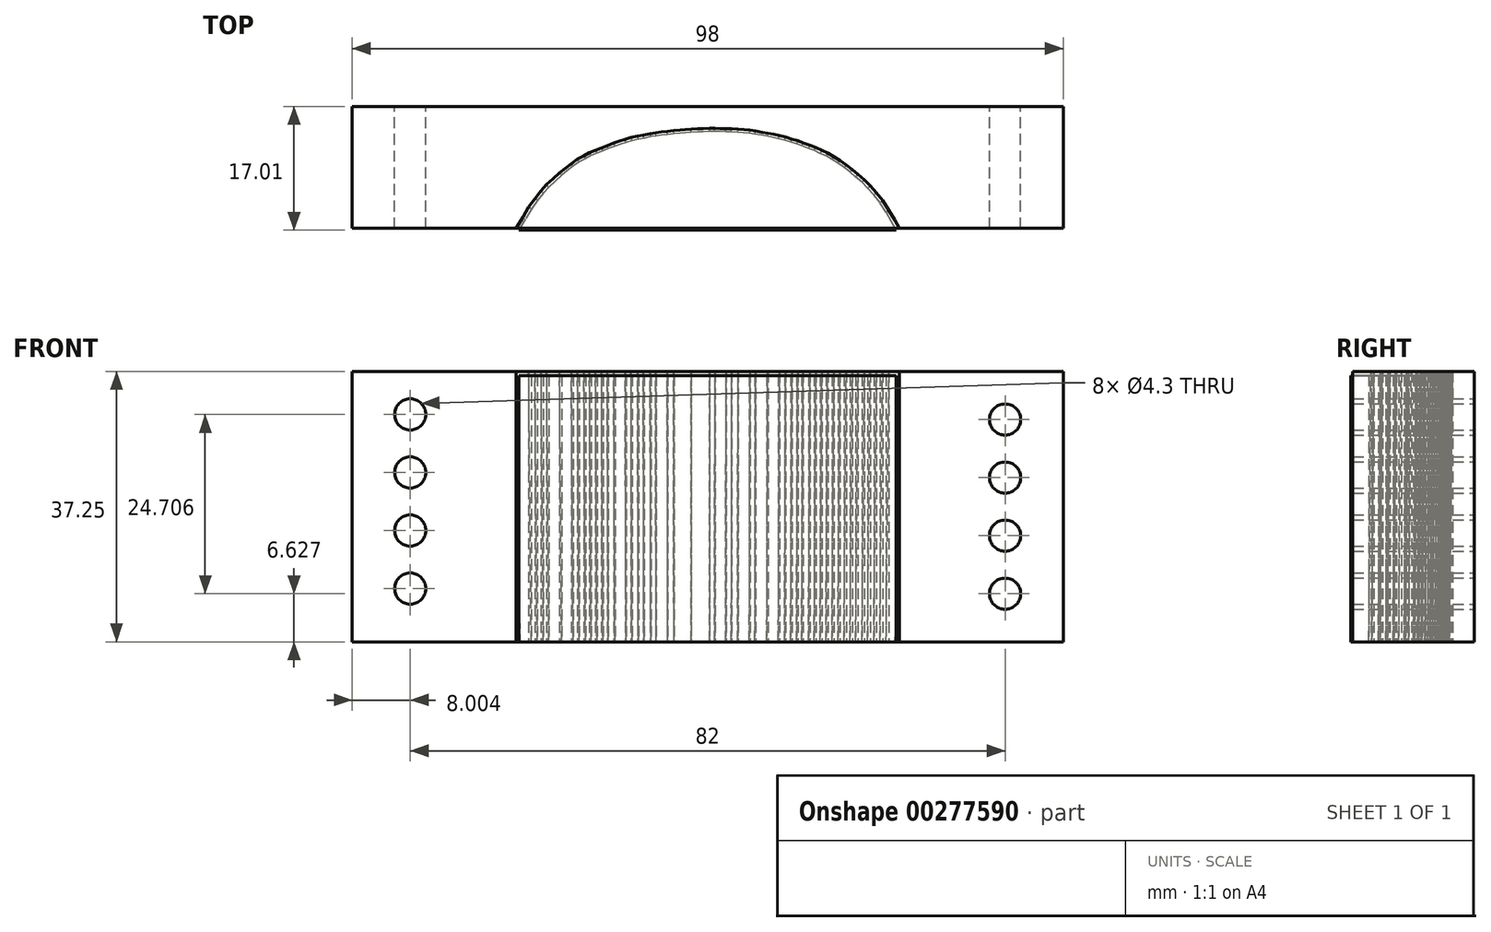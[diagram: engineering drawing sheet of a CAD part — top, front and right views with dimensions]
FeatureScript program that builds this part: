
annotation { "Feature Type Name" : "Feature", "Feature Type Description" : "" }
export const myFeature = defineFeature(function(context is Context, id is Id, definition is map)
    precondition{}
    {
        {
            var Q0;
            Q0=qCreatedBy(makeId("Top.planeOp"),FACE);
            var sketch = newSketch(context, id + "F0", { "sketchPlane" : qUnion([Q0])});
            skLineSegment(sketch, "E0", {"start": v(-9.94, -1.75) * mm, "end": v(-10.2, -1.18) * mm});
            skLineSegment(sketch, "E1", {"start": v(-10.2, -1.18) * mm, "end": v(-10.52, -0.6) * mm});
            skLineSegment(sketch, "E2", {"start": v(-10.52, -0.6) * mm, "end": v(-10.8, -0.09) * mm});
            skLineSegment(sketch, "E3", {"start": v(-10.8, -0.09) * mm, "end": v(-11.13, 0.42) * mm});
            skLineSegment(sketch, "E4", {"start": v(-11.13, 0.42) * mm, "end": v(-11.45, 0.82) * mm});
            skLineSegment(sketch, "E5", {"start": v(-11.45, 0.82) * mm, "end": v(-11.77, 1.2) * mm});
            skLineSegment(sketch, "E6", {"start": v(-11.77, 1.2) * mm, "end": v(-12.06, 1.5) * mm});
            skLineSegment(sketch, "E7", {"start": v(-12.06, 1.5) * mm, "end": v(-12.4, 1.78) * mm});
            skLineSegment(sketch, "E8", {"start": v(-12.4, 1.78) * mm, "end": v(-12.7, 2.03) * mm});
            skLineSegment(sketch, "E9", {"start": v(-12.7, 2.03) * mm, "end": v(-13.01, 2.28) * mm});
            skLineSegment(sketch, "E10", {"start": v(-13.01, 2.28) * mm, "end": v(-13.33, 2.5) * mm});
            skLineSegment(sketch, "E11", {"start": v(-13.33, 2.5) * mm, "end": v(-13.64, 2.7) * mm});
            skLineSegment(sketch, "E12", {"start": v(-13.64, 2.7) * mm, "end": v(-13.96, 2.9) * mm});
            skLineSegment(sketch, "E13", {"start": v(-13.96, 2.9) * mm, "end": v(-14.27, 3.04) * mm});
            skLineSegment(sketch, "E14", {"start": v(-14.27, 3.04) * mm, "end": v(-14.58, 3.2) * mm});
            skLineSegment(sketch, "E15", {"start": v(-14.58, 3.2) * mm, "end": v(-14.88, 3.3) * mm});
            skLineSegment(sketch, "E16", {"start": v(-14.88, 3.3) * mm, "end": v(-15.24, 3.44) * mm});
            skLineSegment(sketch, "E17", {"start": v(-15.24, 3.44) * mm, "end": v(-15.51, 3.55) * mm});
            skLineSegment(sketch, "E18", {"start": v(-15.51, 3.55) * mm, "end": v(-15.82, 3.64) * mm});
            skLineSegment(sketch, "E19", {"start": v(-15.82, 3.64) * mm, "end": v(-16.14, 3.75) * mm});
            skLineSegment(sketch, "E20", {"start": v(-16.14, 3.75) * mm, "end": v(-16.47, 3.83) * mm});
            skLineSegment(sketch, "E21", {"start": v(-16.47, 3.83) * mm, "end": v(-16.76, 3.9) * mm});
            skLineSegment(sketch, "E22", {"start": v(-16.76, 3.9) * mm, "end": v(-17.07, 3.96) * mm});
            skLineSegment(sketch, "E23", {"start": v(-17.07, 3.96) * mm, "end": v(-17.36, 4.01) * mm});
            skLineSegment(sketch, "E24", {"start": v(-17.36, 4.01) * mm, "end": v(-17.7, 4.07) * mm});
            skLineSegment(sketch, "E25", {"start": v(-17.7, 4.07) * mm, "end": v(-18, 4.12) * mm});
            skLineSegment(sketch, "E26", {"start": v(-18, 4.12) * mm, "end": v(-18.32, 4.15) * mm});
            skLineSegment(sketch, "E27", {"start": v(-18.32, 4.15) * mm, "end": v(-18.62, 4.18) * mm});
            skLineSegment(sketch, "E28", {"start": v(-18.62, 4.18) * mm, "end": v(-18.94, 4.2) * mm});
            skLineSegment(sketch, "E29", {"start": v(-18.94, 4.2) * mm, "end": v(-19.25, 4.2) * mm});
            skLineSegment(sketch, "E30", {"start": v(-19.25, 4.2) * mm, "end": v(-19.55, 4.22) * mm});
            skLineSegment(sketch, "E31", {"start": v(-19.55, 4.22) * mm, "end": v(-19.82, 4.23) * mm});
            skLineSegment(sketch, "E32", {"start": v(-19.82, 4.23) * mm, "end": v(-20.1, 4.24) * mm});
            skLineSegment(sketch, "E33", {"start": v(-20.1, 4.24) * mm, "end": v(-20.44, 4.23) * mm});
            skLineSegment(sketch, "E34", {"start": v(-20.44, 4.23) * mm, "end": v(-20.73, 4.21) * mm});
            skLineSegment(sketch, "E35", {"start": v(-20.73, 4.21) * mm, "end": v(-21.06, 4.2) * mm});
            skLineSegment(sketch, "E36", {"start": v(-21.06, 4.2) * mm, "end": v(-21.37, 4.18) * mm});
            skLineSegment(sketch, "E37", {"start": v(-21.37, 4.18) * mm, "end": v(-21.64, 4.16) * mm});
            skLineSegment(sketch, "E38", {"start": v(-21.64, 4.16) * mm, "end": v(-21.98, 4.13) * mm});
            skLineSegment(sketch, "E39", {"start": v(-21.98, 4.13) * mm, "end": v(-22.3, 4.1) * mm});
            skLineSegment(sketch, "E40", {"start": v(-22.3, 4.1) * mm, "end": v(-22.62, 4.06) * mm});
            skLineSegment(sketch, "E41", {"start": v(-22.62, 4.06) * mm, "end": v(-22.92, 4.02) * mm});
            skLineSegment(sketch, "E42", {"start": v(-22.92, 4.02) * mm, "end": v(-23.2, 3.98) * mm});
            skLineSegment(sketch, "E43", {"start": v(-23.2, 3.98) * mm, "end": v(-23.56, 3.9) * mm});
            skLineSegment(sketch, "E44", {"start": v(-23.56, 3.9) * mm, "end": v(-23.86, 3.86) * mm});
            skLineSegment(sketch, "E45", {"start": v(-23.86, 3.86) * mm, "end": v(-24.2, 3.79) * mm});
            skLineSegment(sketch, "E46", {"start": v(-24.2, 3.79) * mm, "end": v(-24.5, 3.69) * mm});
            skLineSegment(sketch, "E47", {"start": v(-24.5, 3.69) * mm, "end": v(-24.8, 3.6) * mm});
            skLineSegment(sketch, "E48", {"start": v(-24.8, 3.6) * mm, "end": v(-25.1, 3.5) * mm});
            skLineSegment(sketch, "E49", {"start": v(-25.1, 3.5) * mm, "end": v(-25.44, 3.38) * mm});
            skLineSegment(sketch, "E50", {"start": v(-25.44, 3.38) * mm, "end": v(-25.73, 3.25) * mm});
            skLineSegment(sketch, "E51", {"start": v(-25.73, 3.25) * mm, "end": v(-26.05, 3.13) * mm});
            skLineSegment(sketch, "E52", {"start": v(-26.05, 3.13) * mm, "end": v(-26.36, 3.01) * mm});
            skLineSegment(sketch, "E53", {"start": v(-26.36, 3.01) * mm, "end": v(-26.66, 2.86) * mm});
            skLineSegment(sketch, "E54", {"start": v(-26.66, 2.86) * mm, "end": v(-26.99, 2.67) * mm});
            skLineSegment(sketch, "E55", {"start": v(-26.99, 2.67) * mm, "end": v(-27.31, 2.46) * mm});
            skLineSegment(sketch, "E56", {"start": v(-27.31, 2.46) * mm, "end": v(-27.61, 2.22) * mm});
            skLineSegment(sketch, "E57", {"start": v(-27.61, 2.22) * mm, "end": v(-27.92, 1.98) * mm});
            skLineSegment(sketch, "E58", {"start": v(-27.92, 1.98) * mm, "end": v(-28.27, 1.67) * mm});
            skLineSegment(sketch, "E59", {"start": v(-28.27, 1.67) * mm, "end": v(-28.6, 1.37) * mm});
            skLineSegment(sketch, "E60", {"start": v(-28.6, 1.37) * mm, "end": v(-28.89, 1.04) * mm});
            skLineSegment(sketch, "E61", {"start": v(-28.89, 1.04) * mm, "end": v(-29.22, 0.65) * mm});
            skLineSegment(sketch, "E62", {"start": v(-29.22, 0.65) * mm, "end": v(-29.54, 0.2) * mm});
            skLineSegment(sketch, "E63", {"start": v(-29.54, 0.2) * mm, "end": v(-29.85, -0.3) * mm});
            skLineSegment(sketch, "E64", {"start": v(-29.85, -0.3) * mm, "end": v(-30.2, -0.9) * mm});
            skLineSegment(sketch, "E65", {"start": v(-30.2, -0.9) * mm, "end": v(-30.45, -1.56) * mm});
            skLineSegment(sketch, "E66", {"start": v(-30.45, -1.56) * mm, "end": v(-9.94, -1.75) * mm, "construction": true});
            skLineSegment(sketch, "E67", {"start": v(-32.25, 10.07) * mm, "end": v(-9.38, 9.9) * mm, "construction": true});
            skLineSegment(sketch, "E68", {"start": v(-32.25, 10.07) * mm, "end": v(-30.45, -1.56) * mm, "construction": true});
            skLineSegment(sketch, "E69", {"start": v(-30.45, -1.56) * mm, "end": v(-9.38, 9.9) * mm, "construction": true});
            skLineSegment(sketch, "E70", {"start": v(-9.38, 9.9) * mm, "end": v(-9.94, -1.75) * mm, "construction": true});
            skLineSegment(sketch, "E71", {"start": v(-33.87, 11.08) * mm, "end": v(-32.25, 10.07) * mm, "construction": true});
            skLineSegment(sketch, "E72", {"start": v(-32.25, 10.07) * mm, "end": v(-7.89, 11.08) * mm, "construction": true});
            skLineSegment(sketch, "E73", {"start": v(-30.2, -0.9) * mm, "end": v(-10.28, -1.04) * mm});
            skLineSegment(sketch, "E74", {"start": v(-32.25, 10.07) * mm, "end": v(-22.42, 10.07) * mm, "construction": true});
            skPoint(sketch, "E75", {"position": v(-20.66, -0.96) * mm});
            skLineSegment(sketch, "E76", {"start": v(-20.62, 4.22) * mm, "end": v(-20.7, -7) * mm, "construction": true});
            skPoint(sketch, "E77", {"position": v(-20.7, -7) * mm});
            skSolve(sketch);
        }
        {
            var Q0;
            {var subQ0=sQuery(id+"F0.wireOp",EDGE,"E2");Q0=makeQuery(id+"F0.imprint","IMPRINT",FACE,{"disambiguationData":[TD([[makeQuery(id+"F0.imprint","IMPRINT",EDGE,{"derivedFrom":subQ0}),1.0]])]});}
            extrude(context, id + "F1", {"entities" : qUnion([Q0]), "depth" : 38.1 * mm * .369});
        }
        {
            var Q0;
            Q0=makeQuery(id+"F1.opExtrude","SWEPT_BODY",BODY,{"disambiguationData":[OSD([sQuery(id+"F0.wireOp",EDGE,"E1"),sQuery(id+"F0.wireOp",EDGE,"E2"),sQuery(id+"F0.wireOp",EDGE,"E3"),sQuery(id+"F0.wireOp",EDGE,"E4"),sQuery(id+"F0.wireOp",EDGE,"E5"),sQuery(id+"F0.wireOp",EDGE,"E6"),sQuery(id+"F0.wireOp",EDGE,"E7"),sQuery(id+"F0.wireOp",EDGE,"E8"),sQuery(id+"F0.wireOp",EDGE,"E9"),sQuery(id+"F0.wireOp",EDGE,"E10"),sQuery(id+"F0.wireOp",EDGE,"E11"),sQuery(id+"F0.wireOp",EDGE,"E12"),sQuery(id+"F0.wireOp",EDGE,"E13"),sQuery(id+"F0.wireOp",EDGE,"E14"),sQuery(id+"F0.wireOp",EDGE,"E15"),sQuery(id+"F0.wireOp",EDGE,"E16"),sQuery(id+"F0.wireOp",EDGE,"E17"),sQuery(id+"F0.wireOp",EDGE,"E18"),sQuery(id+"F0.wireOp",EDGE,"E19"),sQuery(id+"F0.wireOp",EDGE,"E20"),sQuery(id+"F0.wireOp",EDGE,"E21"),sQuery(id+"F0.wireOp",EDGE,"E22"),sQuery(id+"F0.wireOp",EDGE,"E23"),sQuery(id+"F0.wireOp",EDGE,"E24"),sQuery(id+"F0.wireOp",EDGE,"E25"),sQuery(id+"F0.wireOp",EDGE,"E26"),sQuery(id+"F0.wireOp",EDGE,"E27"),sQuery(id+"F0.wireOp",EDGE,"E28"),sQuery(id+"F0.wireOp",EDGE,"E29"),sQuery(id+"F0.wireOp",EDGE,"E30"),sQuery(id+"F0.wireOp",EDGE,"E31"),sQuery(id+"F0.wireOp",EDGE,"E32"),sQuery(id+"F0.wireOp",EDGE,"E33"),sQuery(id+"F0.wireOp",EDGE,"E34"),sQuery(id+"F0.wireOp",EDGE,"E35"),sQuery(id+"F0.wireOp",EDGE,"E36"),sQuery(id+"F0.wireOp",EDGE,"E37"),sQuery(id+"F0.wireOp",EDGE,"E38"),sQuery(id+"F0.wireOp",EDGE,"E39"),sQuery(id+"F0.wireOp",EDGE,"E40"),sQuery(id+"F0.wireOp",EDGE,"E41"),sQuery(id+"F0.wireOp",EDGE,"E42"),sQuery(id+"F0.wireOp",EDGE,"E43"),sQuery(id+"F0.wireOp",EDGE,"E44"),sQuery(id+"F0.wireOp",EDGE,"E45"),sQuery(id+"F0.wireOp",EDGE,"E46"),sQuery(id+"F0.wireOp",EDGE,"E47"),sQuery(id+"F0.wireOp",EDGE,"E48"),sQuery(id+"F0.wireOp",EDGE,"E49"),sQuery(id+"F0.wireOp",EDGE,"E50"),sQuery(id+"F0.wireOp",EDGE,"E51"),sQuery(id+"F0.wireOp",EDGE,"E52"),sQuery(id+"F0.wireOp",EDGE,"E53"),sQuery(id+"F0.wireOp",EDGE,"E54"),sQuery(id+"F0.wireOp",EDGE,"E55"),sQuery(id+"F0.wireOp",EDGE,"E56"),sQuery(id+"F0.wireOp",EDGE,"E57"),sQuery(id+"F0.wireOp",EDGE,"E58"),sQuery(id+"F0.wireOp",EDGE,"E59"),sQuery(id+"F0.wireOp",EDGE,"E60"),sQuery(id+"F0.wireOp",EDGE,"E61"),sQuery(id+"F0.wireOp",EDGE,"E62"),sQuery(id+"F0.wireOp",EDGE,"E63"),sQuery(id+"F0.wireOp",EDGE,"E64"),sQuery(id+"F0.wireOp",EDGE,"E73")])]});
            var Q1;
            Q1=makeQuery(id+"F1.opExtrude","SWEPT_EDGE",EDGE,{"disambiguationData":[OSD([sQuery(id+"F0.wireOp",EDGE,"E64"),sQuery(id+"F0.wireOp",EDGE,"E73")])]});
            transform(context, id + "F2", {"entities" : qUnion([Q0]), "transformType" : TransformType.ROTATION, "transformAxis" : qUnion([Q1]), "angle" : .43 * degree, "oppositeDirection" : true, "makeCopy" : false});
        }
        {
            var Q0;
            Q0=makeQuery(id+"F1.opExtrude","SWEPT_BODY",BODY,{"disambiguationData":[OSD([sQuery(id+"F0.wireOp",EDGE,"E1"),sQuery(id+"F0.wireOp",EDGE,"E2"),sQuery(id+"F0.wireOp",EDGE,"E3"),sQuery(id+"F0.wireOp",EDGE,"E4"),sQuery(id+"F0.wireOp",EDGE,"E5"),sQuery(id+"F0.wireOp",EDGE,"E6"),sQuery(id+"F0.wireOp",EDGE,"E7"),sQuery(id+"F0.wireOp",EDGE,"E8"),sQuery(id+"F0.wireOp",EDGE,"E9"),sQuery(id+"F0.wireOp",EDGE,"E10"),sQuery(id+"F0.wireOp",EDGE,"E11"),sQuery(id+"F0.wireOp",EDGE,"E12"),sQuery(id+"F0.wireOp",EDGE,"E13"),sQuery(id+"F0.wireOp",EDGE,"E14"),sQuery(id+"F0.wireOp",EDGE,"E15"),sQuery(id+"F0.wireOp",EDGE,"E16"),sQuery(id+"F0.wireOp",EDGE,"E17"),sQuery(id+"F0.wireOp",EDGE,"E18"),sQuery(id+"F0.wireOp",EDGE,"E19"),sQuery(id+"F0.wireOp",EDGE,"E20"),sQuery(id+"F0.wireOp",EDGE,"E21"),sQuery(id+"F0.wireOp",EDGE,"E22"),sQuery(id+"F0.wireOp",EDGE,"E23"),sQuery(id+"F0.wireOp",EDGE,"E24"),sQuery(id+"F0.wireOp",EDGE,"E25"),sQuery(id+"F0.wireOp",EDGE,"E26"),sQuery(id+"F0.wireOp",EDGE,"E27"),sQuery(id+"F0.wireOp",EDGE,"E28"),sQuery(id+"F0.wireOp",EDGE,"E29"),sQuery(id+"F0.wireOp",EDGE,"E30"),sQuery(id+"F0.wireOp",EDGE,"E31"),sQuery(id+"F0.wireOp",EDGE,"E32"),sQuery(id+"F0.wireOp",EDGE,"E33"),sQuery(id+"F0.wireOp",EDGE,"E34"),sQuery(id+"F0.wireOp",EDGE,"E35"),sQuery(id+"F0.wireOp",EDGE,"E36"),sQuery(id+"F0.wireOp",EDGE,"E37"),sQuery(id+"F0.wireOp",EDGE,"E38"),sQuery(id+"F0.wireOp",EDGE,"E39"),sQuery(id+"F0.wireOp",EDGE,"E40"),sQuery(id+"F0.wireOp",EDGE,"E41"),sQuery(id+"F0.wireOp",EDGE,"E42"),sQuery(id+"F0.wireOp",EDGE,"E43"),sQuery(id+"F0.wireOp",EDGE,"E44"),sQuery(id+"F0.wireOp",EDGE,"E45"),sQuery(id+"F0.wireOp",EDGE,"E46"),sQuery(id+"F0.wireOp",EDGE,"E47"),sQuery(id+"F0.wireOp",EDGE,"E48"),sQuery(id+"F0.wireOp",EDGE,"E49"),sQuery(id+"F0.wireOp",EDGE,"E50"),sQuery(id+"F0.wireOp",EDGE,"E51"),sQuery(id+"F0.wireOp",EDGE,"E52"),sQuery(id+"F0.wireOp",EDGE,"E53"),sQuery(id+"F0.wireOp",EDGE,"E54"),sQuery(id+"F0.wireOp",EDGE,"E55"),sQuery(id+"F0.wireOp",EDGE,"E56"),sQuery(id+"F0.wireOp",EDGE,"E57"),sQuery(id+"F0.wireOp",EDGE,"E58"),sQuery(id+"F0.wireOp",EDGE,"E59"),sQuery(id+"F0.wireOp",EDGE,"E60"),sQuery(id+"F0.wireOp",EDGE,"E61"),sQuery(id+"F0.wireOp",EDGE,"E62"),sQuery(id+"F0.wireOp",EDGE,"E63"),sQuery(id+"F0.wireOp",EDGE,"E64"),sQuery(id+"F0.wireOp",EDGE,"E73")])]});
            var Q1;
            Q1=sQuery(id+"F0.wireOp",VERTEX,"E77");
            transform(context, id + "F3", {"entities" : qUnion([Q0]), "transformType" : TransformType.SCALE_UNIFORMLY, "scale" : 55.6 / 20.52 * 52.8 / 54.8, "scalePoint" : qUnion([Q1]), "makeCopy" : false});
        }
        {
            var Q0;
            Q0=makeQuery(id+"F1.opExtrude","SWEPT_BODY",BODY,{"disambiguationData":[OSD([sQuery(id+"F0.wireOp",EDGE,"E1"),sQuery(id+"F0.wireOp",EDGE,"E2"),sQuery(id+"F0.wireOp",EDGE,"E3"),sQuery(id+"F0.wireOp",EDGE,"E4"),sQuery(id+"F0.wireOp",EDGE,"E5"),sQuery(id+"F0.wireOp",EDGE,"E6"),sQuery(id+"F0.wireOp",EDGE,"E7"),sQuery(id+"F0.wireOp",EDGE,"E8"),sQuery(id+"F0.wireOp",EDGE,"E9"),sQuery(id+"F0.wireOp",EDGE,"E10"),sQuery(id+"F0.wireOp",EDGE,"E11"),sQuery(id+"F0.wireOp",EDGE,"E12"),sQuery(id+"F0.wireOp",EDGE,"E13"),sQuery(id+"F0.wireOp",EDGE,"E14"),sQuery(id+"F0.wireOp",EDGE,"E15"),sQuery(id+"F0.wireOp",EDGE,"E16"),sQuery(id+"F0.wireOp",EDGE,"E17"),sQuery(id+"F0.wireOp",EDGE,"E18"),sQuery(id+"F0.wireOp",EDGE,"E19"),sQuery(id+"F0.wireOp",EDGE,"E20"),sQuery(id+"F0.wireOp",EDGE,"E21"),sQuery(id+"F0.wireOp",EDGE,"E22"),sQuery(id+"F0.wireOp",EDGE,"E23"),sQuery(id+"F0.wireOp",EDGE,"E24"),sQuery(id+"F0.wireOp",EDGE,"E25"),sQuery(id+"F0.wireOp",EDGE,"E26"),sQuery(id+"F0.wireOp",EDGE,"E27"),sQuery(id+"F0.wireOp",EDGE,"E28"),sQuery(id+"F0.wireOp",EDGE,"E29"),sQuery(id+"F0.wireOp",EDGE,"E30"),sQuery(id+"F0.wireOp",EDGE,"E31"),sQuery(id+"F0.wireOp",EDGE,"E32"),sQuery(id+"F0.wireOp",EDGE,"E33"),sQuery(id+"F0.wireOp",EDGE,"E34"),sQuery(id+"F0.wireOp",EDGE,"E35"),sQuery(id+"F0.wireOp",EDGE,"E36"),sQuery(id+"F0.wireOp",EDGE,"E37"),sQuery(id+"F0.wireOp",EDGE,"E38"),sQuery(id+"F0.wireOp",EDGE,"E39"),sQuery(id+"F0.wireOp",EDGE,"E40"),sQuery(id+"F0.wireOp",EDGE,"E41"),sQuery(id+"F0.wireOp",EDGE,"E42"),sQuery(id+"F0.wireOp",EDGE,"E43"),sQuery(id+"F0.wireOp",EDGE,"E44"),sQuery(id+"F0.wireOp",EDGE,"E45"),sQuery(id+"F0.wireOp",EDGE,"E46"),sQuery(id+"F0.wireOp",EDGE,"E47"),sQuery(id+"F0.wireOp",EDGE,"E48"),sQuery(id+"F0.wireOp",EDGE,"E49"),sQuery(id+"F0.wireOp",EDGE,"E50"),sQuery(id+"F0.wireOp",EDGE,"E51"),sQuery(id+"F0.wireOp",EDGE,"E52"),sQuery(id+"F0.wireOp",EDGE,"E53"),sQuery(id+"F0.wireOp",EDGE,"E54"),sQuery(id+"F0.wireOp",EDGE,"E55"),sQuery(id+"F0.wireOp",EDGE,"E56"),sQuery(id+"F0.wireOp",EDGE,"E57"),sQuery(id+"F0.wireOp",EDGE,"E58"),sQuery(id+"F0.wireOp",EDGE,"E59"),sQuery(id+"F0.wireOp",EDGE,"E60"),sQuery(id+"F0.wireOp",EDGE,"E61"),sQuery(id+"F0.wireOp",EDGE,"E62"),sQuery(id+"F0.wireOp",EDGE,"E63"),sQuery(id+"F0.wireOp",EDGE,"E64"),sQuery(id+"F0.wireOp",EDGE,"E73")])]});
            var Q1;
            Q1=sQuery(id+"F0.wireOp",VERTEX,"E77");
            transform(context, id + "F4", {"entities" : qUnion([Q0]), "transformType" : TransformType.SCALE_UNIFORMLY, "scale" : 61.76 / 60.85, "scalePoint" : qUnion([Q1]), "makeCopy" : true});
        }
        {
            var Q0;
            Q0=makeQuery(id+"F1.opExtrude","CAP_FACE",FACE,{"disambiguationData":[OSD([sQuery(id+"F0.wireOp",EDGE,"E1"),sQuery(id+"F0.wireOp",EDGE,"E2"),sQuery(id+"F0.wireOp",EDGE,"E3"),sQuery(id+"F0.wireOp",EDGE,"E4"),sQuery(id+"F0.wireOp",EDGE,"E5"),sQuery(id+"F0.wireOp",EDGE,"E6"),sQuery(id+"F0.wireOp",EDGE,"E7"),sQuery(id+"F0.wireOp",EDGE,"E8"),sQuery(id+"F0.wireOp",EDGE,"E9"),sQuery(id+"F0.wireOp",EDGE,"E10"),sQuery(id+"F0.wireOp",EDGE,"E11"),sQuery(id+"F0.wireOp",EDGE,"E12"),sQuery(id+"F0.wireOp",EDGE,"E13"),sQuery(id+"F0.wireOp",EDGE,"E14"),sQuery(id+"F0.wireOp",EDGE,"E15"),sQuery(id+"F0.wireOp",EDGE,"E16"),sQuery(id+"F0.wireOp",EDGE,"E17"),sQuery(id+"F0.wireOp",EDGE,"E18"),sQuery(id+"F0.wireOp",EDGE,"E19"),sQuery(id+"F0.wireOp",EDGE,"E20"),sQuery(id+"F0.wireOp",EDGE,"E21"),sQuery(id+"F0.wireOp",EDGE,"E22"),sQuery(id+"F0.wireOp",EDGE,"E23"),sQuery(id+"F0.wireOp",EDGE,"E24"),sQuery(id+"F0.wireOp",EDGE,"E25"),sQuery(id+"F0.wireOp",EDGE,"E26"),sQuery(id+"F0.wireOp",EDGE,"E27"),sQuery(id+"F0.wireOp",EDGE,"E28"),sQuery(id+"F0.wireOp",EDGE,"E29"),sQuery(id+"F0.wireOp",EDGE,"E30"),sQuery(id+"F0.wireOp",EDGE,"E31"),sQuery(id+"F0.wireOp",EDGE,"E32"),sQuery(id+"F0.wireOp",EDGE,"E33"),sQuery(id+"F0.wireOp",EDGE,"E34"),sQuery(id+"F0.wireOp",EDGE,"E35"),sQuery(id+"F0.wireOp",EDGE,"E36"),sQuery(id+"F0.wireOp",EDGE,"E37"),sQuery(id+"F0.wireOp",EDGE,"E38"),sQuery(id+"F0.wireOp",EDGE,"E39"),sQuery(id+"F0.wireOp",EDGE,"E40"),sQuery(id+"F0.wireOp",EDGE,"E41"),sQuery(id+"F0.wireOp",EDGE,"E42"),sQuery(id+"F0.wireOp",EDGE,"E43"),sQuery(id+"F0.wireOp",EDGE,"E44"),sQuery(id+"F0.wireOp",EDGE,"E45"),sQuery(id+"F0.wireOp",EDGE,"E46"),sQuery(id+"F0.wireOp",EDGE,"E47"),sQuery(id+"F0.wireOp",EDGE,"E48"),sQuery(id+"F0.wireOp",EDGE,"E49"),sQuery(id+"F0.wireOp",EDGE,"E50"),sQuery(id+"F0.wireOp",EDGE,"E51"),sQuery(id+"F0.wireOp",EDGE,"E52"),sQuery(id+"F0.wireOp",EDGE,"E53"),sQuery(id+"F0.wireOp",EDGE,"E54"),sQuery(id+"F0.wireOp",EDGE,"E55"),sQuery(id+"F0.wireOp",EDGE,"E56"),sQuery(id+"F0.wireOp",EDGE,"E57"),sQuery(id+"F0.wireOp",EDGE,"E58"),sQuery(id+"F0.wireOp",EDGE,"E59"),sQuery(id+"F0.wireOp",EDGE,"E60"),sQuery(id+"F0.wireOp",EDGE,"E61"),sQuery(id+"F0.wireOp",EDGE,"E62"),sQuery(id+"F0.wireOp",EDGE,"E63"),sQuery(id+"F0.wireOp",EDGE,"E64"),sQuery(id+"F0.wireOp",EDGE,"E73")])],"isStart":true});
            var Q1;
            Q1=makeQuery(id+"F4.opPattern","COPY",FACE,{"derivedFrom":makeQuery(id+"F1.opExtrude","CAP_FACE",FACE,{"disambiguationData":[OSD([sQuery(id+"F0.wireOp",EDGE,"E1"),sQuery(id+"F0.wireOp",EDGE,"E2"),sQuery(id+"F0.wireOp",EDGE,"E3"),sQuery(id+"F0.wireOp",EDGE,"E4"),sQuery(id+"F0.wireOp",EDGE,"E5"),sQuery(id+"F0.wireOp",EDGE,"E6"),sQuery(id+"F0.wireOp",EDGE,"E7"),sQuery(id+"F0.wireOp",EDGE,"E8"),sQuery(id+"F0.wireOp",EDGE,"E9"),sQuery(id+"F0.wireOp",EDGE,"E10"),sQuery(id+"F0.wireOp",EDGE,"E11"),sQuery(id+"F0.wireOp",EDGE,"E12"),sQuery(id+"F0.wireOp",EDGE,"E13"),sQuery(id+"F0.wireOp",EDGE,"E14"),sQuery(id+"F0.wireOp",EDGE,"E15"),sQuery(id+"F0.wireOp",EDGE,"E16"),sQuery(id+"F0.wireOp",EDGE,"E17"),sQuery(id+"F0.wireOp",EDGE,"E18"),sQuery(id+"F0.wireOp",EDGE,"E19"),sQuery(id+"F0.wireOp",EDGE,"E20"),sQuery(id+"F0.wireOp",EDGE,"E21"),sQuery(id+"F0.wireOp",EDGE,"E22"),sQuery(id+"F0.wireOp",EDGE,"E23"),sQuery(id+"F0.wireOp",EDGE,"E24"),sQuery(id+"F0.wireOp",EDGE,"E25"),sQuery(id+"F0.wireOp",EDGE,"E26"),sQuery(id+"F0.wireOp",EDGE,"E27"),sQuery(id+"F0.wireOp",EDGE,"E28"),sQuery(id+"F0.wireOp",EDGE,"E29"),sQuery(id+"F0.wireOp",EDGE,"E30"),sQuery(id+"F0.wireOp",EDGE,"E31"),sQuery(id+"F0.wireOp",EDGE,"E32"),sQuery(id+"F0.wireOp",EDGE,"E33"),sQuery(id+"F0.wireOp",EDGE,"E34"),sQuery(id+"F0.wireOp",EDGE,"E35"),sQuery(id+"F0.wireOp",EDGE,"E36"),sQuery(id+"F0.wireOp",EDGE,"E37"),sQuery(id+"F0.wireOp",EDGE,"E38"),sQuery(id+"F0.wireOp",EDGE,"E39"),sQuery(id+"F0.wireOp",EDGE,"E40"),sQuery(id+"F0.wireOp",EDGE,"E41"),sQuery(id+"F0.wireOp",EDGE,"E42"),sQuery(id+"F0.wireOp",EDGE,"E43"),sQuery(id+"F0.wireOp",EDGE,"E44"),sQuery(id+"F0.wireOp",EDGE,"E45"),sQuery(id+"F0.wireOp",EDGE,"E46"),sQuery(id+"F0.wireOp",EDGE,"E47"),sQuery(id+"F0.wireOp",EDGE,"E48"),sQuery(id+"F0.wireOp",EDGE,"E49"),sQuery(id+"F0.wireOp",EDGE,"E50"),sQuery(id+"F0.wireOp",EDGE,"E51"),sQuery(id+"F0.wireOp",EDGE,"E52"),sQuery(id+"F0.wireOp",EDGE,"E53"),sQuery(id+"F0.wireOp",EDGE,"E54"),sQuery(id+"F0.wireOp",EDGE,"E55"),sQuery(id+"F0.wireOp",EDGE,"E56"),sQuery(id+"F0.wireOp",EDGE,"E57"),sQuery(id+"F0.wireOp",EDGE,"E58"),sQuery(id+"F0.wireOp",EDGE,"E59"),sQuery(id+"F0.wireOp",EDGE,"E60"),sQuery(id+"F0.wireOp",EDGE,"E61"),sQuery(id+"F0.wireOp",EDGE,"E62"),sQuery(id+"F0.wireOp",EDGE,"E63"),sQuery(id+"F0.wireOp",EDGE,"E64"),sQuery(id+"F0.wireOp",EDGE,"E73")])],"isStart":false}),"instanceName":"1"});
            loft(context, id + "F5", {"sheetProfilesArray" : [{ "sheetProfileEntities" : qUnion([Q0]) }, { "sheetProfileEntities" : qUnion([Q1]) }]});
        }
        {
            var Q0;
            {var subQ0=sQuery(id+"F0.wireOp",EDGE,"E73");var subQ1=sQuery(id+"F0.wireOp",EDGE,"E64");var subQ2=sQuery(id+"F0.wireOp",EDGE,"E63");var subQ3=sQuery(id+"F0.wireOp",EDGE,"E62");var subQ4=sQuery(id+"F0.wireOp",EDGE,"E61");var subQ5=sQuery(id+"F0.wireOp",EDGE,"E60");var subQ6=sQuery(id+"F0.wireOp",EDGE,"E59");var subQ7=sQuery(id+"F0.wireOp",EDGE,"E58");var subQ8=sQuery(id+"F0.wireOp",EDGE,"E57");var subQ9=sQuery(id+"F0.wireOp",EDGE,"E56");var subQ10=sQuery(id+"F0.wireOp",EDGE,"E55");var subQ11=sQuery(id+"F0.wireOp",EDGE,"E54");var subQ12=sQuery(id+"F0.wireOp",EDGE,"E53");var subQ13=sQuery(id+"F0.wireOp",EDGE,"E52");var subQ14=sQuery(id+"F0.wireOp",EDGE,"E51");var subQ15=sQuery(id+"F0.wireOp",EDGE,"E50");var subQ16=sQuery(id+"F0.wireOp",EDGE,"E49");var subQ17=sQuery(id+"F0.wireOp",EDGE,"E48");var subQ18=sQuery(id+"F0.wireOp",EDGE,"E47");var subQ19=sQuery(id+"F0.wireOp",EDGE,"E46");var subQ20=sQuery(id+"F0.wireOp",EDGE,"E45");var subQ21=sQuery(id+"F0.wireOp",EDGE,"E44");var subQ22=sQuery(id+"F0.wireOp",EDGE,"E43");var subQ23=sQuery(id+"F0.wireOp",EDGE,"E42");var subQ24=sQuery(id+"F0.wireOp",EDGE,"E41");var subQ25=sQuery(id+"F0.wireOp",EDGE,"E40");var subQ26=sQuery(id+"F0.wireOp",EDGE,"E39");var subQ27=sQuery(id+"F0.wireOp",EDGE,"E38");var subQ28=sQuery(id+"F0.wireOp",EDGE,"E37");var subQ29=sQuery(id+"F0.wireOp",EDGE,"E36");var subQ30=sQuery(id+"F0.wireOp",EDGE,"E35");var subQ31=sQuery(id+"F0.wireOp",EDGE,"E34");var subQ32=sQuery(id+"F0.wireOp",EDGE,"E33");var subQ33=sQuery(id+"F0.wireOp",EDGE,"E32");var subQ34=sQuery(id+"F0.wireOp",EDGE,"E31");var subQ35=sQuery(id+"F0.wireOp",EDGE,"E30");var subQ36=sQuery(id+"F0.wireOp",EDGE,"E29");var subQ37=sQuery(id+"F0.wireOp",EDGE,"E28");var subQ38=sQuery(id+"F0.wireOp",EDGE,"E27");var subQ39=sQuery(id+"F0.wireOp",EDGE,"E26");var subQ40=sQuery(id+"F0.wireOp",EDGE,"E25");var subQ41=sQuery(id+"F0.wireOp",EDGE,"E24");var subQ42=sQuery(id+"F0.wireOp",EDGE,"E23");var subQ43=sQuery(id+"F0.wireOp",EDGE,"E22");var subQ44=sQuery(id+"F0.wireOp",EDGE,"E21");var subQ45=sQuery(id+"F0.wireOp",EDGE,"E20");var subQ46=sQuery(id+"F0.wireOp",EDGE,"E19");var subQ47=sQuery(id+"F0.wireOp",EDGE,"E18");var subQ48=sQuery(id+"F0.wireOp",EDGE,"E17");var subQ49=sQuery(id+"F0.wireOp",EDGE,"E16");var subQ50=sQuery(id+"F0.wireOp",EDGE,"E15");var subQ51=sQuery(id+"F0.wireOp",EDGE,"E14");var subQ52=sQuery(id+"F0.wireOp",EDGE,"E13");var subQ53=sQuery(id+"F0.wireOp",EDGE,"E12");var subQ54=sQuery(id+"F0.wireOp",EDGE,"E11");var subQ55=sQuery(id+"F0.wireOp",EDGE,"E10");var subQ56=sQuery(id+"F0.wireOp",EDGE,"E9");var subQ57=sQuery(id+"F0.wireOp",EDGE,"E8");var subQ58=sQuery(id+"F0.wireOp",EDGE,"E7");var subQ59=sQuery(id+"F0.wireOp",EDGE,"E6");var subQ60=sQuery(id+"F0.wireOp",EDGE,"E5");var subQ61=sQuery(id+"F0.wireOp",EDGE,"E4");var subQ62=sQuery(id+"F0.wireOp",EDGE,"E3");var subQ63=sQuery(id+"F0.wireOp",EDGE,"E2");var subQ64=sQuery(id+"F0.wireOp",EDGE,"E1");Q0=makeQuery(id+"F5.opLoft","CAP_FACE",FACE,{"disambiguationData":[OSD([subQ64,subQ63,subQ62,subQ61,subQ60,subQ59,subQ58,subQ57,subQ56,subQ55,subQ54,subQ53,subQ52,subQ51,subQ50,subQ49,subQ48,subQ47,subQ46,subQ45,subQ44,subQ43,subQ42,subQ41,subQ40,subQ39,subQ38,subQ37,subQ36,subQ35,subQ34,subQ33,subQ32,subQ31,subQ30,subQ29,subQ28,subQ27,subQ26,subQ25,subQ24,subQ23,subQ22,subQ21,subQ20,subQ19,subQ18,subQ17,subQ16,subQ15,subQ14,subQ13,subQ12,subQ11,subQ10,subQ9,subQ8,subQ7,subQ6,subQ5,subQ4,subQ3,subQ2,subQ1,subQ0]),TDD([makeQuery(id+"F4.opPattern","COPY",FACE,{"derivedFrom":makeQuery(id+"F1.opExtrude","CAP_FACE",FACE,{"disambiguationData":[OSD([subQ64,subQ63,subQ62,subQ61,subQ60,subQ59,subQ58,subQ57,subQ56,subQ55,subQ54,subQ53,subQ52,subQ51,subQ50,subQ49,subQ48,subQ47,subQ46,subQ45,subQ44,subQ43,subQ42,subQ41,subQ40,subQ39,subQ38,subQ37,subQ36,subQ35,subQ34,subQ33,subQ32,subQ31,subQ30,subQ29,subQ28,subQ27,subQ26,subQ25,subQ24,subQ23,subQ22,subQ21,subQ20,subQ19,subQ18,subQ17,subQ16,subQ15,subQ14,subQ13,subQ12,subQ11,subQ10,subQ9,subQ8,subQ7,subQ6,subQ5,subQ4,subQ3,subQ2,subQ1,subQ0])],"isStart":false}),"instanceName":"1"})])],"isStart":true});}
            var sketch = newSketch(context, id + "F6", { "sketchPlane" : qUnion([Q0])});
            skLineSegment(sketch, "E78.bottom", {"start": v(-68.48, 25.98) * mm, "end": v(29.52, 25.98) * mm});
            skLineSegment(sketch, "E78.top", {"start": v(-68.48, 9.2) * mm, "end": v(29.52, 9.2) * mm});
            skLineSegment(sketch, "E78.left", {"start": v(-68.48, 25.98) * mm, "end": v(-68.48, 9.2) * mm});
            skLineSegment(sketch, "E78.right", {"start": v(29.52, 25.98) * mm, "end": v(29.52, 9.2) * mm});
            skPoint(sketch, "E79", {"position": v(-19.48, 9.2) * mm});
            skPoint(sketch, "E80", {"position": v(-19.48, 25.98) * mm});
            skLineSegment(sketch, "E81", {"start": v(-19.48, 25.98) * mm, "end": v(-19.48, 9.2) * mm, "construction": true});
            skSolve(sketch);
        }
        {
            var Q0;
            Q0=makeQuery(id+"F6.imprint","IMPRINT",FACE,{"disambiguationData":[TD([[makeQuery(id+"F6.imprint","IMPRINT",EDGE,{"derivedFrom":sQuery(id+"F6.wireOp",EDGE,"E78.bottom")}),-1.0]])]});
            var Q1;
            {var subQ33=sQuery(id+"F0.wireOp",EDGE,"E3");var subQ39=sQuery(id+"F0.wireOp",EDGE,"E2");var subQ40=sQuery(id+"F0.wireOp",EDGE,"E1");Q1=makeQuery(id+"F6.imprint","IMPRINT",FACE,{"disambiguationData":[TD([[makeQuery(id+"F6.imprint","IMPRINT",EDGE,{"derivedFrom":makeQuery(id+"F5.opLoft","MID_CAP_EDGE",EDGE,{"disambiguationData":[OSD([subQ40,subQ39,subQ33])],"capPos":1.0})}),1.0]])]});}
            var Q2;
            {var subQ0=sQuery(id+"F0.wireOp",EDGE,"E73");var subQ1=sQuery(id+"F0.wireOp",EDGE,"E64");var subQ2=sQuery(id+"F0.wireOp",EDGE,"E63");var subQ3=sQuery(id+"F0.wireOp",EDGE,"E62");var subQ4=sQuery(id+"F0.wireOp",EDGE,"E61");var subQ5=sQuery(id+"F0.wireOp",EDGE,"E60");var subQ6=sQuery(id+"F0.wireOp",EDGE,"E59");var subQ7=sQuery(id+"F0.wireOp",EDGE,"E58");var subQ8=sQuery(id+"F0.wireOp",EDGE,"E57");var subQ9=sQuery(id+"F0.wireOp",EDGE,"E56");var subQ10=sQuery(id+"F0.wireOp",EDGE,"E55");var subQ11=sQuery(id+"F0.wireOp",EDGE,"E54");var subQ12=sQuery(id+"F0.wireOp",EDGE,"E53");var subQ13=sQuery(id+"F0.wireOp",EDGE,"E52");var subQ14=sQuery(id+"F0.wireOp",EDGE,"E51");var subQ15=sQuery(id+"F0.wireOp",EDGE,"E50");var subQ16=sQuery(id+"F0.wireOp",EDGE,"E49");var subQ17=sQuery(id+"F0.wireOp",EDGE,"E48");var subQ18=sQuery(id+"F0.wireOp",EDGE,"E47");var subQ19=sQuery(id+"F0.wireOp",EDGE,"E46");var subQ20=sQuery(id+"F0.wireOp",EDGE,"E45");var subQ21=sQuery(id+"F0.wireOp",EDGE,"E44");var subQ22=sQuery(id+"F0.wireOp",EDGE,"E43");var subQ23=sQuery(id+"F0.wireOp",EDGE,"E42");var subQ24=sQuery(id+"F0.wireOp",EDGE,"E41");var subQ25=sQuery(id+"F0.wireOp",EDGE,"E40");var subQ26=sQuery(id+"F0.wireOp",EDGE,"E39");var subQ27=sQuery(id+"F0.wireOp",EDGE,"E38");var subQ28=sQuery(id+"F0.wireOp",EDGE,"E37");var subQ29=sQuery(id+"F0.wireOp",EDGE,"E36");var subQ30=sQuery(id+"F0.wireOp",EDGE,"E35");var subQ31=sQuery(id+"F0.wireOp",EDGE,"E34");var subQ32=sQuery(id+"F0.wireOp",EDGE,"E33");var subQ33=sQuery(id+"F0.wireOp",EDGE,"E32");var subQ34=sQuery(id+"F0.wireOp",EDGE,"E31");var subQ35=sQuery(id+"F0.wireOp",EDGE,"E30");var subQ36=sQuery(id+"F0.wireOp",EDGE,"E29");var subQ37=sQuery(id+"F0.wireOp",EDGE,"E28");var subQ38=sQuery(id+"F0.wireOp",EDGE,"E27");var subQ39=sQuery(id+"F0.wireOp",EDGE,"E26");var subQ40=sQuery(id+"F0.wireOp",EDGE,"E25");var subQ41=sQuery(id+"F0.wireOp",EDGE,"E24");var subQ42=sQuery(id+"F0.wireOp",EDGE,"E23");var subQ43=sQuery(id+"F0.wireOp",EDGE,"E22");var subQ44=sQuery(id+"F0.wireOp",EDGE,"E21");var subQ45=sQuery(id+"F0.wireOp",EDGE,"E20");var subQ46=sQuery(id+"F0.wireOp",EDGE,"E19");var subQ47=sQuery(id+"F0.wireOp",EDGE,"E18");var subQ48=sQuery(id+"F0.wireOp",EDGE,"E17");var subQ49=sQuery(id+"F0.wireOp",EDGE,"E16");var subQ50=sQuery(id+"F0.wireOp",EDGE,"E15");var subQ51=sQuery(id+"F0.wireOp",EDGE,"E14");var subQ52=sQuery(id+"F0.wireOp",EDGE,"E13");var subQ53=sQuery(id+"F0.wireOp",EDGE,"E12");var subQ54=sQuery(id+"F0.wireOp",EDGE,"E11");var subQ55=sQuery(id+"F0.wireOp",EDGE,"E10");var subQ56=sQuery(id+"F0.wireOp",EDGE,"E9");var subQ57=sQuery(id+"F0.wireOp",EDGE,"E8");var subQ58=sQuery(id+"F0.wireOp",EDGE,"E7");var subQ59=sQuery(id+"F0.wireOp",EDGE,"E6");var subQ60=sQuery(id+"F0.wireOp",EDGE,"E5");var subQ61=sQuery(id+"F0.wireOp",EDGE,"E4");var subQ62=sQuery(id+"F0.wireOp",EDGE,"E3");var subQ63=sQuery(id+"F0.wireOp",EDGE,"E2");var subQ64=sQuery(id+"F0.wireOp",EDGE,"E1");Q2=makeQuery(id+"F5.opLoft","CAP_FACE",FACE,{"disambiguationData":[OSD([subQ64,subQ63,subQ62,subQ61,subQ60,subQ59,subQ58,subQ57,subQ56,subQ55,subQ54,subQ53,subQ52,subQ51,subQ50,subQ49,subQ48,subQ47,subQ46,subQ45,subQ44,subQ43,subQ42,subQ41,subQ40,subQ39,subQ38,subQ37,subQ36,subQ35,subQ34,subQ33,subQ32,subQ31,subQ30,subQ29,subQ28,subQ27,subQ26,subQ25,subQ24,subQ23,subQ22,subQ21,subQ20,subQ19,subQ18,subQ17,subQ16,subQ15,subQ14,subQ13,subQ12,subQ11,subQ10,subQ9,subQ8,subQ7,subQ6,subQ5,subQ4,subQ3,subQ2,subQ1,subQ0]),TDD([makeQuery(id+"F1.opExtrude","CAP_FACE",FACE,{"disambiguationData":[OSD([subQ64,subQ63,subQ62,subQ61,subQ60,subQ59,subQ58,subQ57,subQ56,subQ55,subQ54,subQ53,subQ52,subQ51,subQ50,subQ49,subQ48,subQ47,subQ46,subQ45,subQ44,subQ43,subQ42,subQ41,subQ40,subQ39,subQ38,subQ37,subQ36,subQ35,subQ34,subQ33,subQ32,subQ31,subQ30,subQ29,subQ28,subQ27,subQ26,subQ25,subQ24,subQ23,subQ22,subQ21,subQ20,subQ19,subQ18,subQ17,subQ16,subQ15,subQ14,subQ13,subQ12,subQ11,subQ10,subQ9,subQ8,subQ7,subQ6,subQ5,subQ4,subQ3,subQ2,subQ1,subQ0])],"isStart":true})])],"isStart":true});}
            extrude(context, id + "F7", {"entities" : qUnion([Q0, Q1]), "endBound" : BoundingType.UP_TO_SURFACE, "oppositeDirection" : true, "endBoundEntityFace" : qUnion([Q2]), "depth" : 25 * mm});
        }
        {
            var Q0;
            Q0=makeQuery(id+"F5.opLoft","SWEPT_BODY",BODY,{"disambiguationData":[OSD([sQuery(id+"F0.wireOp",EDGE,"E1"),sQuery(id+"F0.wireOp",EDGE,"E2"),sQuery(id+"F0.wireOp",EDGE,"E3"),sQuery(id+"F0.wireOp",EDGE,"E4"),sQuery(id+"F0.wireOp",EDGE,"E5"),sQuery(id+"F0.wireOp",EDGE,"E6"),sQuery(id+"F0.wireOp",EDGE,"E7"),sQuery(id+"F0.wireOp",EDGE,"E8"),sQuery(id+"F0.wireOp",EDGE,"E9"),sQuery(id+"F0.wireOp",EDGE,"E10"),sQuery(id+"F0.wireOp",EDGE,"E11"),sQuery(id+"F0.wireOp",EDGE,"E12"),sQuery(id+"F0.wireOp",EDGE,"E13"),sQuery(id+"F0.wireOp",EDGE,"E14"),sQuery(id+"F0.wireOp",EDGE,"E15"),sQuery(id+"F0.wireOp",EDGE,"E16"),sQuery(id+"F0.wireOp",EDGE,"E17"),sQuery(id+"F0.wireOp",EDGE,"E18"),sQuery(id+"F0.wireOp",EDGE,"E19"),sQuery(id+"F0.wireOp",EDGE,"E20"),sQuery(id+"F0.wireOp",EDGE,"E21"),sQuery(id+"F0.wireOp",EDGE,"E22"),sQuery(id+"F0.wireOp",EDGE,"E23"),sQuery(id+"F0.wireOp",EDGE,"E24"),sQuery(id+"F0.wireOp",EDGE,"E25"),sQuery(id+"F0.wireOp",EDGE,"E26"),sQuery(id+"F0.wireOp",EDGE,"E27"),sQuery(id+"F0.wireOp",EDGE,"E28"),sQuery(id+"F0.wireOp",EDGE,"E29"),sQuery(id+"F0.wireOp",EDGE,"E30"),sQuery(id+"F0.wireOp",EDGE,"E31"),sQuery(id+"F0.wireOp",EDGE,"E32"),sQuery(id+"F0.wireOp",EDGE,"E33"),sQuery(id+"F0.wireOp",EDGE,"E34"),sQuery(id+"F0.wireOp",EDGE,"E35"),sQuery(id+"F0.wireOp",EDGE,"E36"),sQuery(id+"F0.wireOp",EDGE,"E37"),sQuery(id+"F0.wireOp",EDGE,"E38"),sQuery(id+"F0.wireOp",EDGE,"E39"),sQuery(id+"F0.wireOp",EDGE,"E40"),sQuery(id+"F0.wireOp",EDGE,"E41"),sQuery(id+"F0.wireOp",EDGE,"E42"),sQuery(id+"F0.wireOp",EDGE,"E43"),sQuery(id+"F0.wireOp",EDGE,"E44"),sQuery(id+"F0.wireOp",EDGE,"E45"),sQuery(id+"F0.wireOp",EDGE,"E46"),sQuery(id+"F0.wireOp",EDGE,"E47"),sQuery(id+"F0.wireOp",EDGE,"E48"),sQuery(id+"F0.wireOp",EDGE,"E49"),sQuery(id+"F0.wireOp",EDGE,"E50"),sQuery(id+"F0.wireOp",EDGE,"E51"),sQuery(id+"F0.wireOp",EDGE,"E52"),sQuery(id+"F0.wireOp",EDGE,"E53"),sQuery(id+"F0.wireOp",EDGE,"E54"),sQuery(id+"F0.wireOp",EDGE,"E55"),sQuery(id+"F0.wireOp",EDGE,"E56"),sQuery(id+"F0.wireOp",EDGE,"E57"),sQuery(id+"F0.wireOp",EDGE,"E58"),sQuery(id+"F0.wireOp",EDGE,"E59"),sQuery(id+"F0.wireOp",EDGE,"E60"),sQuery(id+"F0.wireOp",EDGE,"E61"),sQuery(id+"F0.wireOp",EDGE,"E62"),sQuery(id+"F0.wireOp",EDGE,"E63"),sQuery(id+"F0.wireOp",EDGE,"E64"),sQuery(id+"F0.wireOp",EDGE,"E73")])]});
            var Q1;
            Q1=makeQuery(id+"F7.opExtrude","SWEPT_BODY",BODY,{"disambiguationData":[OSD([sQuery(id+"F6.wireOp",EDGE,"E78.bottom"),sQuery(id+"F6.wireOp",EDGE,"E78.top"),sQuery(id+"F6.wireOp",EDGE,"E78.left"),sQuery(id+"F6.wireOp",EDGE,"E78.right")])]});
            booleanBodies(context, id + "F8", {"operationType" : BooleanOperationType.SUBTRACTION, "tools" : qUnion([Q0]), "targets" : qUnion([Q1])});
        }
        {
            var Q0;
            Q0=makeQuery(id+"F7.opExtrude","SWEPT_FACE",FACE,{"disambiguationData":[OSD([sQuery(id+"F6.wireOp",EDGE,"E78.bottom")])]});
            var sketch = newSketch(context, id + "F9", { "sketchPlane" : qUnion([Q0])});
            skCircle(sketch, "E82", {"center": v(-21.52, 30.63) * mm, "radius": 2.15 * mm});
            skCircle(sketch, "E83", {"center": v(60.48, 31.33) * mm, "radius": 2.15 * mm});
            skCircle(sketch, "E84.0.1.0", {"center": v(-21.52, 22.63) * mm, "radius": 2.15 * mm});
            skCircle(sketch, "E84.0.1.1", {"center": v(60.48, 23.33) * mm, "radius": 2.15 * mm});
            skCircle(sketch, "E84.0.2.0", {"center": v(-21.52, 14.63) * mm, "radius": 2.15 * mm});
            skCircle(sketch, "E84.0.2.1", {"center": v(60.48, 15.33) * mm, "radius": 2.15 * mm});
            skCircle(sketch, "E84.0.3.0", {"center": v(-21.52, 6.63) * mm, "radius": 2.15 * mm});
            skCircle(sketch, "E84.0.3.1", {"center": v(60.48, 7.33) * mm, "radius": 2.15 * mm});
            skLineSegment(sketch, "E84.direction1", {"start": v(-21.52, 30.63) * mm, "end": v(7.43, 30.63) * mm, "construction": true});
            skLineSegment(sketch, "E84.direction2", {"start": v(-21.52, 30.63) * mm, "end": v(-21.52, 22.63) * mm, "construction": true});
            skSolve(sketch);
        }
        {
            var Q0;
            Q0 = qSketchRegion(id + "F9", true);
            extrude(context, id + "F10", {"entities" : qUnion([Q0]), "operationType" : NewBodyOperationType.REMOVE, "endBound" : BoundingType.THROUGH_ALL, "oppositeDirection" : true, "depth" : 25 * mm});
        }
    });
